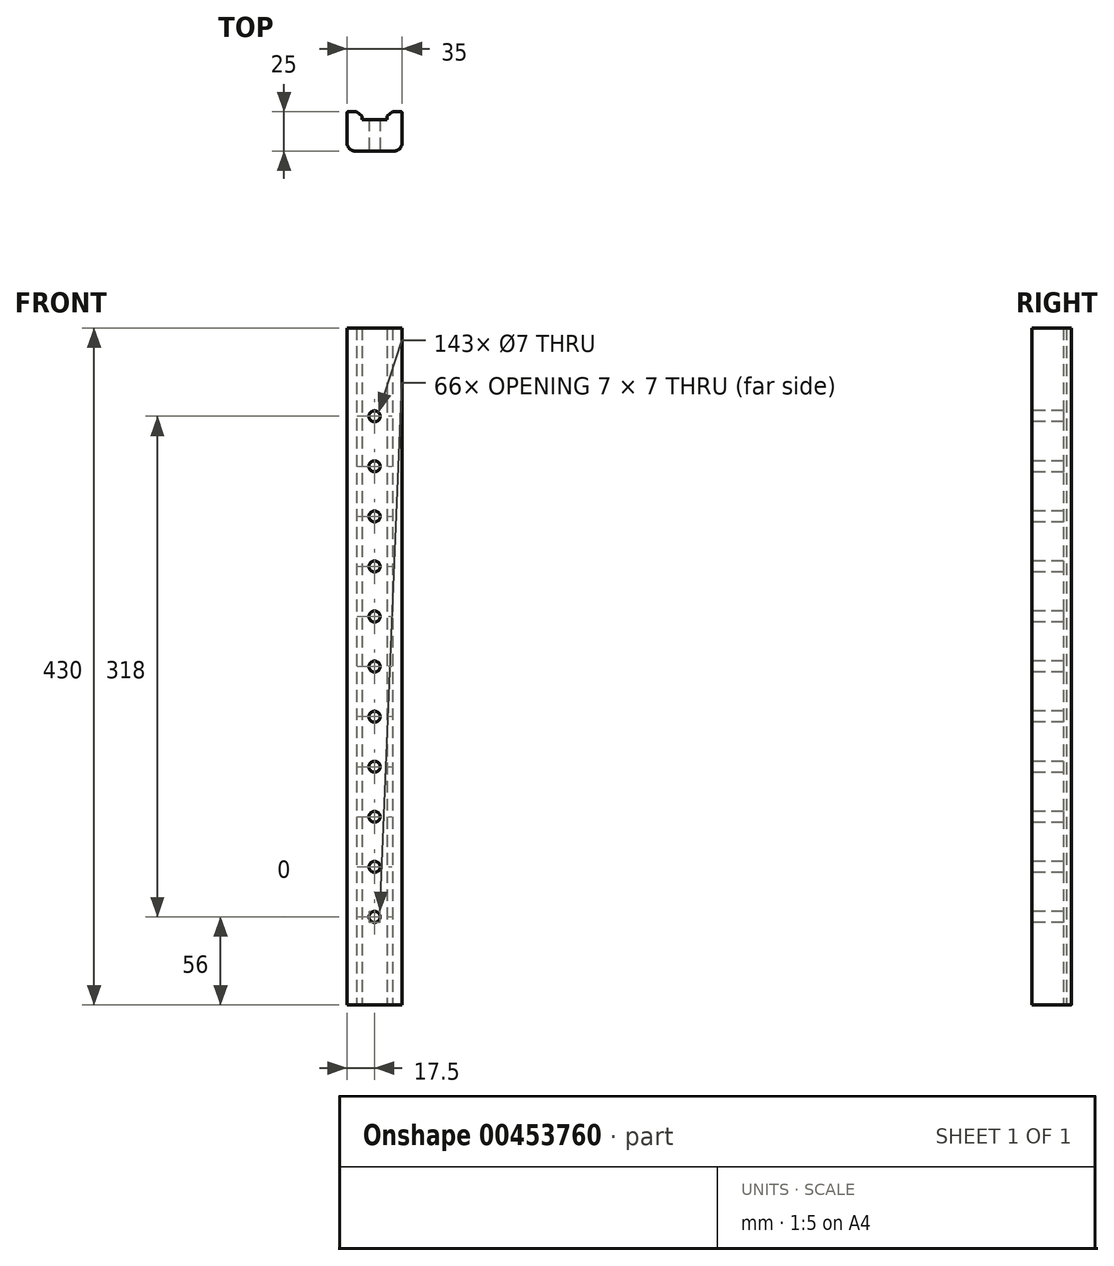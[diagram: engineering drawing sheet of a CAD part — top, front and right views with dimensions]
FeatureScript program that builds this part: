
annotation { "Feature Type Name" : "Feature", "Feature Type Description" : "" }
export const myFeature = defineFeature(function(context is Context, id is Id, definition is map)
    precondition{}
    {
        {
            var Q0;
            Q0=qCreatedBy(makeId("Top.planeOp"),FACE);
            var sketch = newSketch(context, id + "F0", { "sketchPlane" : qUnion([Q0])});
            skLineSegment(sketch, "E0", {"start": v(-5, 0) * mm, "end": v(-30, 0) * mm});
            skLineSegment(sketch, "E1", {"start": v(-35, 5) * mm, "end": v(-35, 24) * mm});
            skLineSegment(sketch, "E2", {"start": v(0, 24) * mm, "end": v(0, 5) * mm});
            skLineSegment(sketch, "E3", {"start": v(-17.5, 20) * mm, "end": v(-9.5, 20) * mm});
            skLineSegment(sketch, "E4", {"start": v(-17.5, 20) * mm, "end": v(-25.5, 20) * mm});
            skLineSegment(sketch, "E5", {"start": v(-25.5, 20) * mm, "end": v(-25.5, 22) * mm});
            skLineSegment(sketch, "E6", {"start": v(-9.5, 20) * mm, "end": v(-9.5, 22) * mm});
            skLineSegment(sketch, "E7", {"start": v(-34, 25) * mm, "end": v(-29, 25) * mm});
            skLineSegment(sketch, "E8", {"start": v(-1, 25) * mm, "end": v(-6, 25) * mm});
            skLineSegment(sketch, "E9", {"start": v(-29, 25) * mm, "end": v(-25.5, 22) * mm});
            skLineSegment(sketch, "E10", {"start": v(-6, 25) * mm, "end": v(-9.5, 22) * mm});
            skPoint(sketch, "E11.visualSharp", {"position": v(-35, 0) * mm});
            skArc(sketch, "E11.filletArc", {"start": v(-35, 5) * mm, "mid": v(-33.54, 1.46) * mm, "end": v(-30, 0) * mm});
            skPoint(sketch, "E12.visualSharp", {"position": v(0, 0) * mm});
            skArc(sketch, "E12.filletArc", {"start": v(-5, 0) * mm, "mid": v(-1.46, 1.46) * mm, "end": v(0, 5) * mm});
            skPoint(sketch, "E13.visualSharp", {"position": v(-35, 25) * mm});
            skArc(sketch, "E13.filletArc", {"start": v(-34, 25) * mm, "mid": v(-34.7, 24.7) * mm, "end": v(-35, 24) * mm});
            skPoint(sketch, "E14.visualSharp", {"position": v(0, 25) * mm});
            skArc(sketch, "E14.filletArc", {"start": v(0, 24) * mm, "mid": v(-0.3, 24.7) * mm, "end": v(-1, 25) * mm});
            skSolve(sketch);
        }
        {
            var Q0;
            Q0=makeQuery(id+"F0.imprint","IMPRINT",FACE,{"disambiguationData":[TD([[makeQuery(id+"F0.imprint","IMPRINT",EDGE,{"derivedFrom":sQuery(id+"F0.wireOp",EDGE,"E0")}),-1.0]])]});
            extrude(context, id + "F1", {"entities" : qUnion([Q0]), "depth" : 430 * mm});
        }
        {
            var Q0;
            Q0=makeQuery(id+"F1.opExtrude","SWEPT_FACE",FACE,{"disambiguationData":[OSD([sQuery(id+"F0.wireOp",EDGE,"E0")])]});
            var sketch = newSketch(context, id + "F2", { "sketchPlane" : qUnion([Q0])});
            skLineSegment(sketch, "E15", {"start": v(-17.5, 430) * mm, "end": v(-17.5, 0) * mm, "construction": true});
            skCircle(sketch, "E16", {"center": v(-17.5, 374) * mm, "radius": 3.5 * mm});
            skCircle(sketch, "E17.1.0.0", {"center": v(-17.5, 342.2) * mm, "radius": 3.5 * mm});
            skCircle(sketch, "E17.2.0.0", {"center": v(-17.5, 310.4) * mm, "radius": 3.5 * mm});
            skCircle(sketch, "E17.3.0.0", {"center": v(-17.5, 278.6) * mm, "radius": 3.5 * mm});
            skCircle(sketch, "E17.4.0.0", {"center": v(-17.5, 246.8) * mm, "radius": 3.5 * mm});
            skCircle(sketch, "E17.5.0.0", {"center": v(-17.5, 215) * mm, "radius": 3.5 * mm});
            skCircle(sketch, "E17.6.0.0", {"center": v(-17.5, 183.2) * mm, "radius": 3.5 * mm});
            skCircle(sketch, "E17.7.0.0", {"center": v(-17.5, 151.4) * mm, "radius": 3.5 * mm});
            skCircle(sketch, "E17.8.0.0", {"center": v(-17.5, 119.6) * mm, "radius": 3.5 * mm});
            skCircle(sketch, "E17.9.0.0", {"center": v(-17.5, 87.8) * mm, "radius": 3.5 * mm});
            skCircle(sketch, "E17.10.0.0", {"center": v(-17.5, 56) * mm, "radius": 3.5 * mm});
            skLineSegment(sketch, "E17.direction1", {"start": v(-17.5, 374) * mm, "end": v(-17.5, 342.2) * mm, "construction": true});
            skSolve(sketch);
        }
        {
            var Q0;
            Q0=sQuery(id+"F2.wireOp",VERTEX,"E16.center");
            var Q1;
            Q1=sQuery(id+"F2.wireOp",VERTEX,"E17.1.0.0.center");
            var Q2;
            Q2=sQuery(id+"F2.wireOp",VERTEX,"E17.2.0.0.center");
            var Q3;
            Q3=sQuery(id+"F2.wireOp",VERTEX,"E17.3.0.0.center");
            var Q4;
            Q4=sQuery(id+"F2.wireOp",VERTEX,"E17.4.0.0.center");
            var Q5;
            Q5=sQuery(id+"F2.wireOp",VERTEX,"E17.5.0.0.center");
            var Q6;
            Q6=sQuery(id+"F2.wireOp",VERTEX,"E17.6.0.0.center");
            var Q7;
            Q7=sQuery(id+"F2.wireOp",VERTEX,"E17.7.0.0.center");
            var Q8;
            Q8=sQuery(id+"F2.wireOp",VERTEX,"E17.8.0.0.center");
            var Q9;
            Q9=sQuery(id+"F2.wireOp",VERTEX,"E17.9.0.0.center");
            var Q10;
            Q10=sQuery(id+"F2.wireOp",VERTEX,"E17.10.0.0.center");
            var Q11;
            Q11=makeQuery(id+"F1.opExtrude","SWEPT_BODY",BODY,{"disambiguationData":[OSD([sQuery(id+"F0.wireOp",EDGE,"E0"),sQuery(id+"F0.wireOp",EDGE,"E1"),sQuery(id+"F0.wireOp",EDGE,"E2"),sQuery(id+"F0.wireOp",EDGE,"E3"),sQuery(id+"F0.wireOp",EDGE,"E4"),sQuery(id+"F0.wireOp",EDGE,"E5"),sQuery(id+"F0.wireOp",EDGE,"E6"),sQuery(id+"F0.wireOp",EDGE,"E7"),sQuery(id+"F0.wireOp",EDGE,"E8"),sQuery(id+"F0.wireOp",EDGE,"E9"),sQuery(id+"F0.wireOp",EDGE,"E10"),sQuery(id+"F0.wireOp",EDGE,"E11.filletArc"),sQuery(id+"F0.wireOp",EDGE,"E12.filletArc"),sQuery(id+"F0.wireOp",EDGE,"E13.filletArc"),sQuery(id+"F0.wireOp",EDGE,"E14.filletArc")])]});
            hole(context, id + "F3", {"style" : HoleStyle.SIMPLE, "endStyle" : HoleEndStyle.THROUGH, "holeDiameter" : 7 * mm, "isTappedThrough" : true, "tappedDepth" : 12 * mm, "tapClearance" : 3, "locations" : qUnion([Q0, Q1, Q2, Q3, Q4, Q5, Q6, Q7, Q8, Q9, Q10]), "scope" : qUnion([Q11])});
        }
    });
